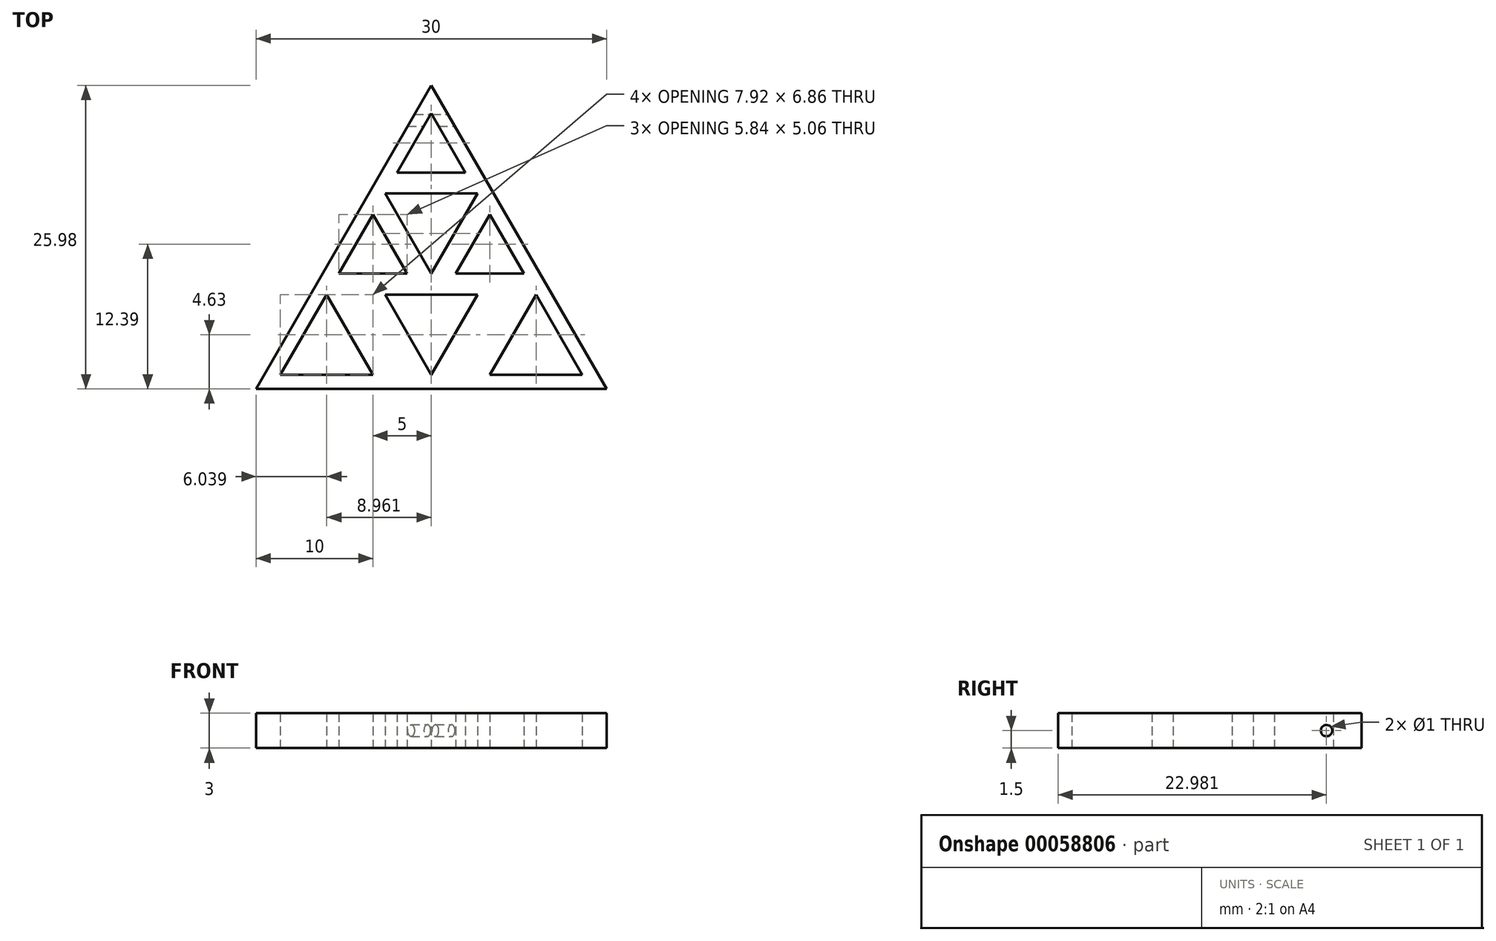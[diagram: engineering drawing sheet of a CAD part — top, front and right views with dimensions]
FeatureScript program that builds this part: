
annotation { "Feature Type Name" : "Feature", "Feature Type Description" : "" }
export const myFeature = defineFeature(function(context is Context, id is Id, definition is map)
    precondition{}
    {
        {
            var Q0;
            Q0=qCreatedBy(makeId("Top.planeOp"),FACE);
            var sketch = newSketch(context, id + "F0", { "sketchPlane" : qUnion([Q0])});
            skLineSegment(sketch, "E0", {"start": v(-15, 0) * mm, "end": v(15, 0) * mm});
            skLineSegment(sketch, "E1", {"start": v(15, 0) * mm, "end": v(0, 25.98) * mm});
            skPoint(sketch, "E1.endSnap0", {"position": v(0, 0) * mm});
            skLineSegment(sketch, "E2", {"start": v(-5, 17.32) * mm, "end": v(5, 17.32) * mm, "construction": true});
            skLineSegment(sketch, "E3", {"start": v(-10, 8.66) * mm, "end": v(10, 8.66) * mm, "construction": true});
            skLineSegment(sketch, "E4", {"start": v(-15, 0) * mm, "end": v(-10, 8.66) * mm});
            skLineSegment(sketch, "E5", {"start": v(-10, 8.66) * mm, "end": v(-5, 17.32) * mm});
            skLineSegment(sketch, "E6", {"start": v(-5, 17.32) * mm, "end": v(0, 25.98) * mm});
            skLineSegment(sketch, "E7", {"start": v(0, 25.98) * mm, "end": v(0, 0) * mm, "construction": true});
            skLineSegment(sketch, "E8", {"start": v(0, 23.58) * mm, "end": v(-2.92, 18.52) * mm});
            skLineSegment(sketch, "E9", {"start": v(-2.92, 18.52) * mm, "end": v(2.92, 18.52) * mm});
            skLineSegment(sketch, "E10", {"start": v(2.92, 18.52) * mm, "end": v(0, 23.58) * mm});
            skLineSegment(sketch, "E11", {"start": v(-7.92, 9.86) * mm, "end": v(-2.08, 9.86) * mm});
            skLineSegment(sketch, "E12", {"start": v(-2.08, 9.86) * mm, "end": v(-5, 14.92) * mm});
            skLineSegment(sketch, "E13", {"start": v(-5, 14.92) * mm, "end": v(-7.92, 9.86) * mm});
            skLineSegment(sketch, "E14.MirrorCS", {"start": v(2.08, 9.86) * mm, "end": v(5, 14.92) * mm});
            skLineSegment(sketch, "E15.MirrorCS", {"start": v(5, 14.92) * mm, "end": v(7.92, 9.86) * mm});
            skLineSegment(sketch, "E16.MirrorCS", {"start": v(7.92, 9.86) * mm, "end": v(2.08, 9.86) * mm});
            skLineSegment(sketch, "E17", {"start": v(-5, 14.92) * mm, "end": v(-2.92, 18.52) * mm, "construction": true});
            skLineSegment(sketch, "E18", {"start": v(0, 9.86) * mm, "end": v(-3.96, 16.72) * mm});
            skLineSegment(sketch, "E19", {"start": v(-3.96, 16.72) * mm, "end": v(0, 16.72) * mm});
            skLineSegment(sketch, "E20.MirrorCS", {"start": v(3.96, 16.72) * mm, "end": v(0, 16.72) * mm});
            skLineSegment(sketch, "E21.MirrorCS", {"start": v(0, 9.86) * mm, "end": v(3.96, 16.72) * mm});
            skLineSegment(sketch, "E22", {"start": v(-12.92, 1.2) * mm, "end": v(-5, 1.2) * mm});
            skLineSegment(sketch, "E23", {"start": v(-5, 1.2) * mm, "end": v(-8.96, 8.06) * mm});
            skLineSegment(sketch, "E24", {"start": v(-8.96, 8.06) * mm, "end": v(-12.92, 1.2) * mm});
            skLineSegment(sketch, "E25", {"start": v(-2.92, 18.52) * mm, "end": v(-2.92, 16.72) * mm, "construction": true});
            skLineSegment(sketch, "E26", {"start": v(-10.35, 8.06) * mm, "end": v(10.35, 8.06) * mm, "construction": true});
            skLineSegment(sketch, "E27", {"start": v(-7.92, 9.86) * mm, "end": v(-7.92, 8.06) * mm, "construction": true});
            skLineSegment(sketch, "E28.MirrorCS", {"start": v(5, 1.2) * mm, "end": v(8.96, 8.06) * mm});
            skLineSegment(sketch, "E29.MirrorCS", {"start": v(8.96, 8.06) * mm, "end": v(12.92, 1.2) * mm});
            skLineSegment(sketch, "E30.MirrorCS", {"start": v(12.92, 1.2) * mm, "end": v(5, 1.2) * mm});
            skLineSegment(sketch, "E31", {"start": v(3.96, 8.06) * mm, "end": v(0, 1.2) * mm});
            skLineSegment(sketch, "E32", {"start": v(3.96, 8.06) * mm, "end": v(0, 8.06) * mm});
            skLineSegment(sketch, "E33.MirrorCS", {"start": v(-3.96, 8.06) * mm, "end": v(0, 8.06) * mm});
            skLineSegment(sketch, "E34.MirrorCS", {"start": v(-3.96, 8.06) * mm, "end": v(0, 1.2) * mm});
            skSolve(sketch);
        }
        {
            var Q0;
            Q0=makeQuery(id+"F0.imprint","IMPRINT",FACE,{"disambiguationData":[TD([[makeQuery(id+"F0.imprint","IMPRINT",EDGE,{"derivedFrom":sQuery(id+"F0.wireOp",EDGE,"E0")}),1.0]])]});
            extrude(context, id + "F1", {"entities" : qUnion([Q0]), "depth" : 3 * mm});
        }
        {
            var Q0;
            Q0=qCreatedBy(makeId("Right.planeOp"),FACE);
            var sketch = newSketch(context, id + "F2", { "sketchPlane" : qUnion([Q0])});
            skPoint(sketch, "E35.0", {"position": v(18.52, 3) * mm});
            skPoint(sketch, "E36.0", {"position": v(25.98, 3) * mm});
            skPoint(sketch, "E37.0", {"position": v(25.98, 0) * mm});
            skLineSegment(sketch, "E38.bottom", {"start": v(25.98, 0) * mm, "end": v(18.52, 0) * mm, "construction": true});
            skLineSegment(sketch, "E38.top", {"start": v(25.98, 3) * mm, "end": v(18.52, 3) * mm, "construction": true});
            skLineSegment(sketch, "E38.left", {"start": v(25.98, 0) * mm, "end": v(25.98, 3) * mm, "construction": true});
            skLineSegment(sketch, "E38.right", {"start": v(18.52, 0) * mm, "end": v(18.52, 3) * mm, "construction": true});
            skCircle(sketch, "E39", {"center": v(22.98, 1.5) * mm, "radius": 0.5 * mm});
            skPoint(sketch, "E39.centerSnap0", {"position": v(25.98, 1.5) * mm});
            skLineSegment(sketch, "E40", {"start": v(25.98, 1.5) * mm, "end": v(18.52, 1.5) * mm, "construction": true});
            skLineSegment(sketch, "E41", {"start": v(22.98, 0) * mm, "end": v(22.98, 3) * mm, "construction": true});
            skSolve(sketch);
        }
        {
            var Q0;
            Q0=makeQuery(id+"F2.imprint","IMPRINT",FACE,{"disambiguationData":[TD([[makeQuery(id+"F2.imprint","IMPRINT",EDGE,{"derivedFrom":sQuery(id+"F2.wireOp",EDGE,"E39")}),1.0]])]});
            extrude(context, id + "F3", {"entities" : qUnion([Q0]), "operationType" : NewBodyOperationType.REMOVE, "endBound" : BoundingType.SYMMETRIC, "oppositeDirection" : true, "depth" : 5 * mm, "hasSecondDirection" : true, "secondDirectionOppositeDirection" : false, "secondDirectionDepth" : 25 * mm});
        }
    });
